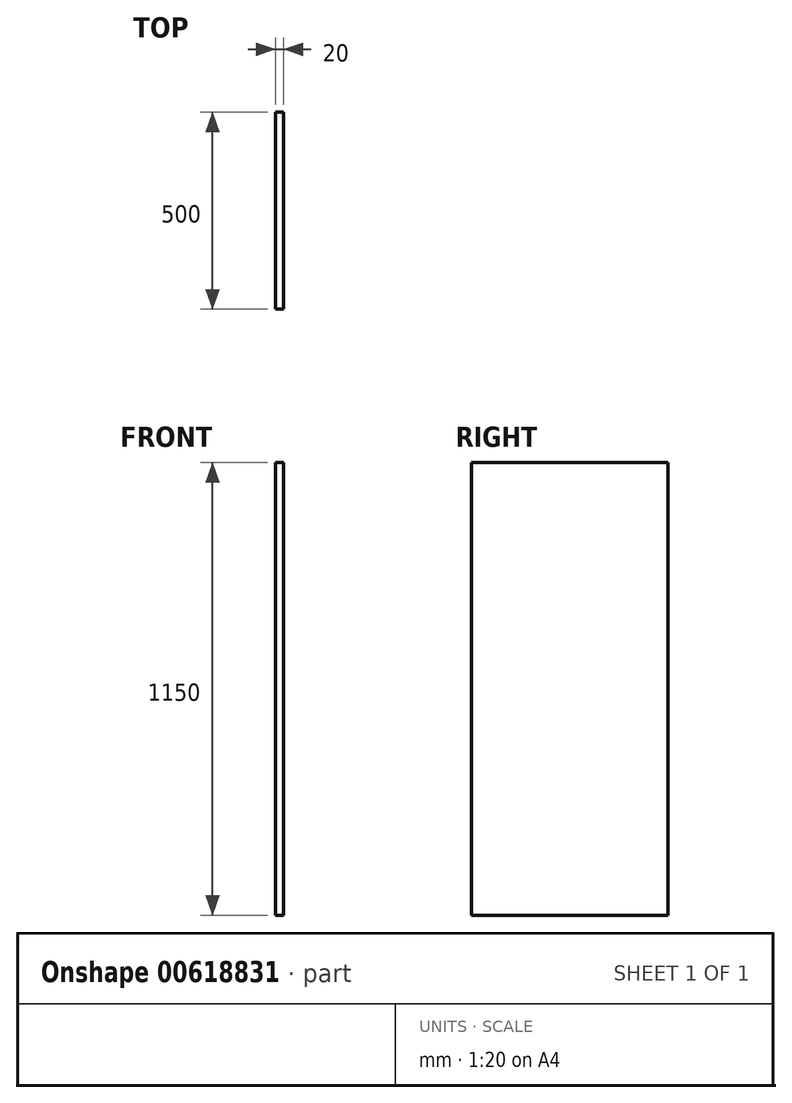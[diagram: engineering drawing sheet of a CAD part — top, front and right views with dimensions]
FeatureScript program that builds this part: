
annotation { "Feature Type Name" : "Feature", "Feature Type Description" : "" }
export const myFeature = defineFeature(function(context is Context, id is Id, definition is map)
    precondition{}
    {
        {
            var Q0;
            Q0=qCreatedBy(makeId("Right.planeOp"),FACE);
            var sketch = newSketch(context, id + "F0", { "sketchPlane" : qUnion([Q0])});
            skLineSegment(sketch, "E0.bottom", {"start": v(-250, 575) * mm, "end": v(250, 575) * mm});
            skLineSegment(sketch, "E0.top", {"start": v(-250, -575) * mm, "end": v(250, -575) * mm});
            skLineSegment(sketch, "E0.left", {"start": v(-250, 575) * mm, "end": v(-250, -575) * mm});
            skLineSegment(sketch, "E0.right", {"start": v(250, 575) * mm, "end": v(250, -575) * mm});
            skPoint(sketch, "E0.middle", {"position": v(0, 0) * mm});
            skSolve(sketch);
        }
        {
            var Q0;
            Q0=makeQuery(id+"F0.imprint","IMPRINT",FACE,{"disambiguationData":[TD([[makeQuery(id+"F0.imprint","IMPRINT",EDGE,{"derivedFrom":sQuery(id+"F0.wireOp",EDGE,"E0.bottom")}),-1.0]])]});
            extrude(context, id + "F1", {"entities" : qUnion([Q0]), "depth" : 20 * mm, "offsetDistance" : 25 * mm});
        }
    });
